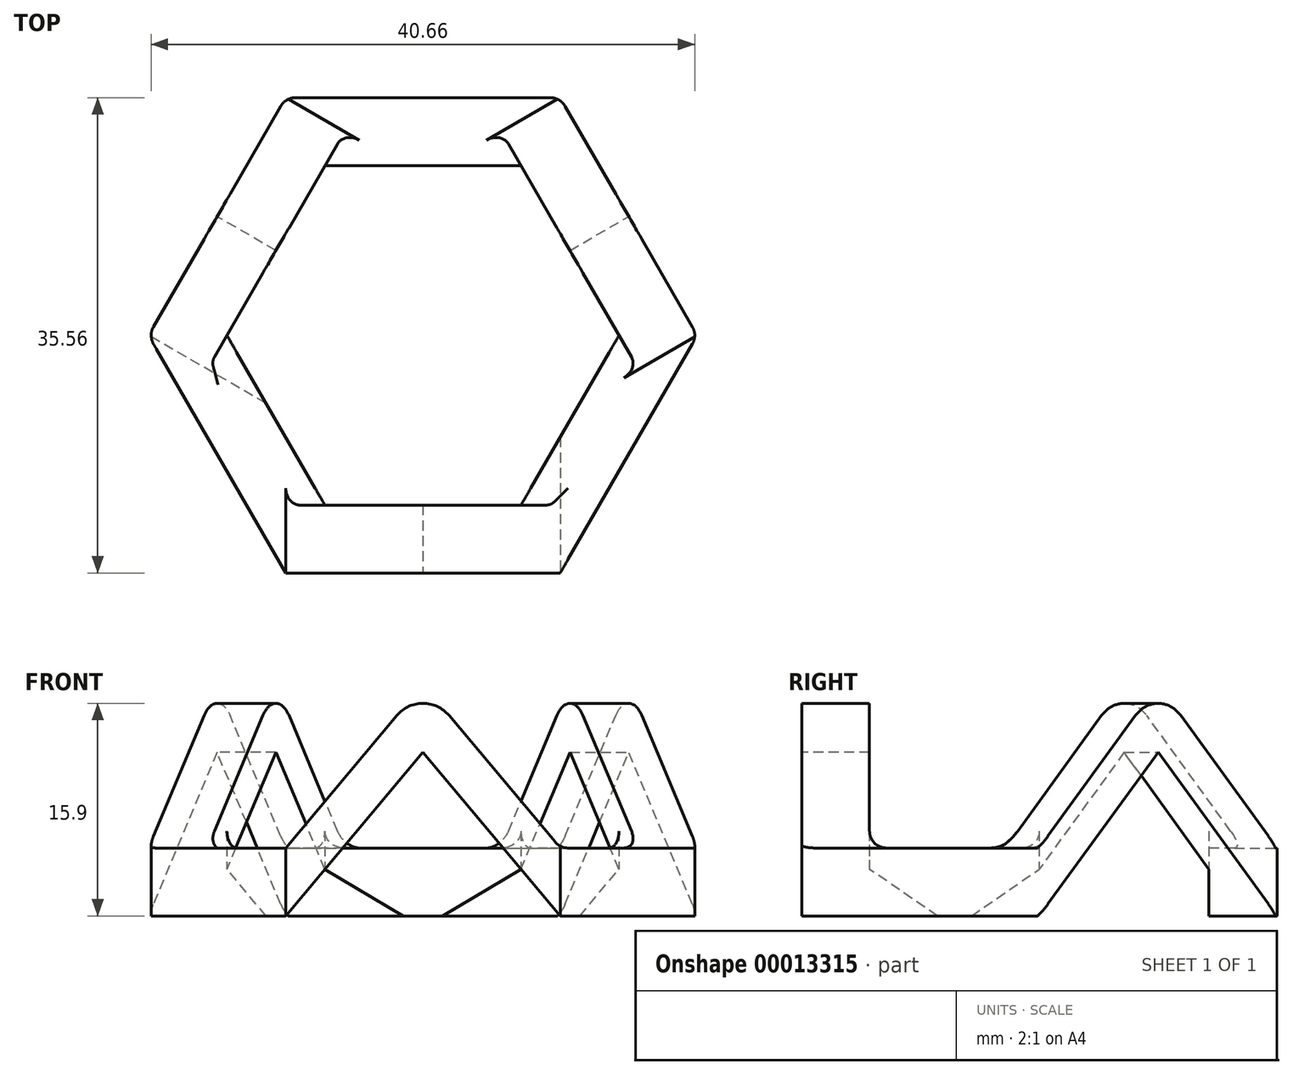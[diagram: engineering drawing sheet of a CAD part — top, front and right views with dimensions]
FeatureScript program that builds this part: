
annotation { "Feature Type Name" : "Feature", "Feature Type Description" : "" }
export const myFeature = defineFeature(function(context is Context, id is Id, definition is map)
    precondition{}
    {
        {
            var Q0;
            Q0=qCreatedBy(makeId("Top.planeOp"),FACE);
            var sketch = newSketch(context, id + "F0", { "sketchPlane" : qUnion([Q0])});
            skCircle(sketch, "E0.cCircle", {"center": v(0, 0) * mm, "radius": 12.7 * mm, "construction": true});
            skLineSegment(sketch, "E0.0", {"start": v(-7.33, 12.7) * mm, "end": v(7.33, 12.7) * mm});
            skLineSegment(sketch, "E0.1", {"start": v(7.33, 12.7) * mm, "end": v(14.66, 0) * mm});
            skLineSegment(sketch, "E0.2", {"start": v(14.66, 0) * mm, "end": v(7.33, -12.7) * mm});
            skLineSegment(sketch, "E0.3", {"start": v(7.33, -12.7) * mm, "end": v(-7.33, -12.7) * mm});
            skLineSegment(sketch, "E0.4", {"start": v(-7.33, -12.7) * mm, "end": v(-14.66, 0) * mm});
            skLineSegment(sketch, "E0.5", {"start": v(-14.66, 0) * mm, "end": v(-7.33, 12.7) * mm});
            skPoint(sketch, "E0.0.midPoint", {"position": v(0, 12.7) * mm});
            skLineSegment(sketch, "E1.0", {"start": v(-20.53, 0) * mm, "end": v(-10.27, 17.78) * mm});
            skLineSegment(sketch, "E1.1", {"start": v(-10.27, -17.78) * mm, "end": v(-20.53, 0) * mm});
            skLineSegment(sketch, "E1.2", {"start": v(10.27, -17.78) * mm, "end": v(-10.27, -17.78) * mm});
            skLineSegment(sketch, "E1.3", {"start": v(20.53, 0) * mm, "end": v(10.27, -17.78) * mm});
            skLineSegment(sketch, "E1.4", {"start": v(10.27, 17.78) * mm, "end": v(20.53, 0) * mm});
            skLineSegment(sketch, "E1.5", {"start": v(-10.27, 17.78) * mm, "end": v(10.27, 17.78) * mm});
            skSolve(sketch);
        }
        {
            var Q0;
            Q0=makeQuery(id+"F0.imprint","IMPRINT",FACE,{"disambiguationData":[TD([[makeQuery(id+"F0.imprint","IMPRINT",EDGE,{"derivedFrom":sQuery(id+"F0.wireOp",EDGE,"E0.0")}),1.0]])]});
            extrude(context, id + "F1", {"entities" : qUnion([Q0]), "depth" : 5.08 * mm});
        }
        {
            var Q0;
            Q0=makeQuery(id+"F1.opExtrude","SWEPT_FACE",FACE,{"disambiguationData":[OSD([sQuery(id+"F0.wireOp",EDGE,"E1.4")])]});
            var sketch = newSketch(context, id + "F2", { "sketchPlane" : qUnion([Q0])});
            skLineSegment(sketch, "E2", {"start": v(-10.27, 0) * mm, "end": v(0, 12.23) * mm});
            skLineSegment(sketch, "E3", {"start": v(10.27, 0) * mm, "end": v(0, 12.23) * mm});
            skLineSegment(sketch, "E4", {"start": v(-10.27, 5.08) * mm, "end": v(0, 17.31) * mm});
            skLineSegment(sketch, "E5", {"start": v(10.27, 5.08) * mm, "end": v(0, 17.31) * mm});
            skSolve(sketch);
        }
        {
            var Q0;
            {var subQ7=sQuery(id+"F2.wireOp",EDGE,"E4");Q0=makeQuery(id+"F2.imprint","IMPRINT",FACE,{"disambiguationData":[TD([[makeQuery(id+"F2.imprint","IMPRINT",EDGE,{"derivedFrom":subQ7}),-1.0]])]});}
            var Q1;
            {var subQ0=sQuery(id+"F0.wireOp",EDGE,"E1.4");var subQ4=makeQuery(id+"F1.opExtrude","SWEPT_EDGE",EDGE,{"disambiguationData":[OSD([sQuery(id+"F0.wireOp",EDGE,"E1.3"),subQ0])]});Q1=makeQuery(id+"F2.imprint","IMPRINT",FACE,{"disambiguationData":[TD([[makeQuery(id+"F2.imprint","IMPRINT",EDGE,{"derivedFrom":subQ4}),1.0]])]});}
            var Q2;
            {var subQ0=sQuery(id+"F0.wireOp",EDGE,"E1.4");var subQ4=makeQuery(id+"F1.opExtrude","SWEPT_EDGE",EDGE,{"disambiguationData":[OSD([subQ0,sQuery(id+"F0.wireOp",EDGE,"E1.5")])]});Q2=makeQuery(id+"F2.imprint","IMPRINT",FACE,{"disambiguationData":[TD([[makeQuery(id+"F2.imprint","IMPRINT",EDGE,{"derivedFrom":subQ4}),-1.0]])]});}
            extrude(context, id + "F3", {"entities" : qUnion([Q0, Q1, Q2]), "operationType" : NewBodyOperationType.ADD, "oppositeDirection" : true, "depth" : 5.08 * mm});
        }
        {
            var Q0;
            {var subQ0=sQuery(id+"F0.wireOp",EDGE,"E1.4");Q0=makeQuery(id+"F3.boolean.opBoolean","MERGE",FACE,{"derivedFrom":[makeQuery(id+"F1.opExtrude","SWEPT_FACE",FACE,{"disambiguationData":[OSD([subQ0])]}),makeQuery(id+"F3.opExtrude","CAP_FACE",FACE,{"disambiguationData":[OSD([sQuery(id+"F0.wireOp",EDGE,"E1.3"),subQ0,sQuery(id+"F0.wireOp",EDGE,"E1.5"),sQuery(id+"F2.wireOp",EDGE,"E2"),sQuery(id+"F2.wireOp",EDGE,"E3"),sQuery(id+"F2.wireOp",EDGE,"E4"),sQuery(id+"F2.wireOp",EDGE,"E5")])],"isStart":true})]});}
            var sketch = newSketch(context, id + "F4", { "sketchPlane" : qUnion([Q0])});
            skLineSegment(sketch, "E6", {"start": v(-10.27, 0) * mm, "end": v(-6, 5.08) * mm});
            skLineSegment(sketch, "E7", {"start": v(10.27, 0) * mm, "end": v(6, 5.08) * mm});
            skSolve(sketch);
        }
        {
            var Q0;
            Q0=makeQuery(id+"F4.imprint","IMPRINT",FACE,{"disambiguationData":[TD([[makeQuery(id+"F4.imprint","IMPRINT",EDGE,{"derivedFrom":sQuery(id+"F4.wireOp",EDGE,"E6")}),-1.0]])]});
            extrude(context, id + "F5", {"entities" : qUnion([Q0]), "operationType" : NewBodyOperationType.REMOVE, "oppositeDirection" : true, "depth" : 10.16 * mm});
        }
        {
            var Q0;
            Q0=makeQuery(id+"F1.opExtrude","SWEPT_FACE",FACE,{"disambiguationData":[OSD([sQuery(id+"F0.wireOp",EDGE,"E1.0")])]});
            var sketch = newSketch(context, id + "F6", { "sketchPlane" : qUnion([Q0])});
            skLineSegment(sketch, "E8", {"start": v(-10.27, 0) * mm, "end": v(0, 12.23) * mm});
            skLineSegment(sketch, "E9", {"start": v(0, 12.23) * mm, "end": v(10.27, 0) * mm});
            skLineSegment(sketch, "E10", {"start": v(-10.27, 5.08) * mm, "end": v(0, 17.31) * mm});
            skLineSegment(sketch, "E11", {"start": v(0, 17.31) * mm, "end": v(10.27, 5.08) * mm});
            skSolve(sketch);
        }
        {
            var Q0;
            {var subQ7=sQuery(id+"F6.wireOp",EDGE,"E10");Q0=makeQuery(id+"F6.imprint","IMPRINT",FACE,{"disambiguationData":[TD([[makeQuery(id+"F6.imprint","IMPRINT",EDGE,{"derivedFrom":subQ7}),-1.0]])]});}
            var Q1;
            {var subQ0=sQuery(id+"F0.wireOp",EDGE,"E1.0");var subQ4=makeQuery(id+"F1.opExtrude","SWEPT_EDGE",EDGE,{"disambiguationData":[OSD([subQ0,sQuery(id+"F0.wireOp",EDGE,"E1.5")])]});Q1=makeQuery(id+"F6.imprint","IMPRINT",FACE,{"disambiguationData":[TD([[makeQuery(id+"F6.imprint","IMPRINT",EDGE,{"derivedFrom":subQ4}),1.0]])]});}
            var Q2;
            {var subQ0=sQuery(id+"F0.wireOp",EDGE,"E1.0");var subQ4=makeQuery(id+"F1.opExtrude","SWEPT_EDGE",EDGE,{"disambiguationData":[OSD([subQ0,sQuery(id+"F0.wireOp",EDGE,"E1.1")])]});Q2=makeQuery(id+"F6.imprint","IMPRINT",FACE,{"disambiguationData":[TD([[makeQuery(id+"F6.imprint","IMPRINT",EDGE,{"derivedFrom":subQ4}),-1.0]])]});}
            extrude(context, id + "F7", {"entities" : qUnion([Q0, Q1, Q2]), "operationType" : NewBodyOperationType.ADD, "oppositeDirection" : true, "depth" : 5.08 * mm});
        }
        {
            var Q0;
            {var subQ0=sQuery(id+"F0.wireOp",EDGE,"E1.0");Q0=makeQuery(id+"F7.boolean.opBoolean","MERGE",FACE,{"derivedFrom":[makeQuery(id+"F1.opExtrude","SWEPT_FACE",FACE,{"disambiguationData":[OSD([subQ0])]}),makeQuery(id+"F7.opExtrude","CAP_FACE",FACE,{"disambiguationData":[OSD([subQ0,sQuery(id+"F0.wireOp",EDGE,"E1.1"),sQuery(id+"F0.wireOp",EDGE,"E1.5"),sQuery(id+"F6.wireOp",EDGE,"E8"),sQuery(id+"F6.wireOp",EDGE,"E9"),sQuery(id+"F6.wireOp",EDGE,"E10"),sQuery(id+"F6.wireOp",EDGE,"E11")])],"isStart":true})]});}
            var sketch = newSketch(context, id + "F8", { "sketchPlane" : qUnion([Q0])});
            skLineSegment(sketch, "E12", {"start": v(-10.27, 0) * mm, "end": v(-6, 5.08) * mm});
            skLineSegment(sketch, "E13", {"start": v(10.27, 0) * mm, "end": v(6, 5.08) * mm});
            skSolve(sketch);
        }
        {
            var Q0;
            Q0 = qSketchRegion(id + "F8", true);
            var Q1;
            Q1=makeQuery(id+"F8.imprint","IMPRINT",FACE,{"disambiguationData":[TD([[makeQuery(id+"F8.imprint","IMPRINT",EDGE,{"derivedFrom":sQuery(id+"F8.wireOp",EDGE,"E12")}),-1.0]])]});
            extrude(context, id + "F9", {"entities" : qUnion([Q0, Q1]), "operationType" : NewBodyOperationType.REMOVE, "oppositeDirection" : true, "depth" : 12.7 * mm});
        }
        {
            var Q0;
            Q0=makeQuery(id+"F1.opExtrude","SWEPT_FACE",FACE,{"disambiguationData":[OSD([sQuery(id+"F0.wireOp",EDGE,"E1.2")])]});
            var sketch = newSketch(context, id + "F10", { "sketchPlane" : qUnion([Q0])});
            skLineSegment(sketch, "E14", {"start": v(-10.27, 0) * mm, "end": v(0, 12.23) * mm});
            skLineSegment(sketch, "E15", {"start": v(0, 12.23) * mm, "end": v(10.27, 0) * mm});
            skLineSegment(sketch, "E16", {"start": v(-10.27, 5.08) * mm, "end": v(0, 17.31) * mm});
            skLineSegment(sketch, "E17", {"start": v(0, 17.31) * mm, "end": v(10.27, 5.08) * mm});
            skSolve(sketch);
        }
        {
            var Q0;
            Q0 = qSketchRegion(id + "F10", true);
            var Q1;
            {var subQ7=sQuery(id+"F10.wireOp",EDGE,"E16");Q1=makeQuery(id+"F10.imprint","IMPRINT",FACE,{"disambiguationData":[TD([[makeQuery(id+"F10.imprint","IMPRINT",EDGE,{"derivedFrom":subQ7}),-1.0]])]});}
            var Q2;
            {var subQ0=sQuery(id+"F0.wireOp",EDGE,"E1.2");var subQ4=makeQuery(id+"F1.opExtrude","SWEPT_EDGE",EDGE,{"disambiguationData":[OSD([sQuery(id+"F0.wireOp",EDGE,"E1.1"),subQ0])]});Q2=makeQuery(id+"F10.imprint","IMPRINT",FACE,{"disambiguationData":[TD([[makeQuery(id+"F10.imprint","IMPRINT",EDGE,{"derivedFrom":subQ4}),1.0]])]});}
            var Q3;
            {var subQ0=sQuery(id+"F0.wireOp",EDGE,"E1.2");var subQ4=makeQuery(id+"F1.opExtrude","SWEPT_EDGE",EDGE,{"disambiguationData":[OSD([subQ0,sQuery(id+"F0.wireOp",EDGE,"E1.3")])]});Q3=makeQuery(id+"F10.imprint","IMPRINT",FACE,{"disambiguationData":[TD([[makeQuery(id+"F10.imprint","IMPRINT",EDGE,{"derivedFrom":subQ4}),-1.0]])]});}
            extrude(context, id + "F11", {"entities" : qUnion([Q0, Q1, Q2, Q3]), "operationType" : NewBodyOperationType.ADD, "oppositeDirection" : true, "depth" : 5.08 * mm});
        }
        {
            var Q0;
            {var subQ0=sQuery(id+"F0.wireOp",EDGE,"E1.2");Q0=makeQuery(id+"F11.boolean.opBoolean","MERGE",FACE,{"derivedFrom":[makeQuery(id+"F1.opExtrude","SWEPT_FACE",FACE,{"disambiguationData":[OSD([subQ0])]}),makeQuery(id+"F11.opExtrude","CAP_FACE",FACE,{"disambiguationData":[OSD([sQuery(id+"F0.wireOp",EDGE,"E1.1"),subQ0,sQuery(id+"F0.wireOp",EDGE,"E1.3"),sQuery(id+"F10.wireOp",EDGE,"E14"),sQuery(id+"F10.wireOp",EDGE,"E15"),sQuery(id+"F10.wireOp",EDGE,"E16"),sQuery(id+"F10.wireOp",EDGE,"E17")])],"isStart":true})]});}
            var sketch = newSketch(context, id + "F12", { "sketchPlane" : qUnion([Q0])});
            skLineSegment(sketch, "E18", {"start": v(-10.27, 0) * mm, "end": v(-6, 5.08) * mm});
            skLineSegment(sketch, "E19", {"start": v(10.27, 0) * mm, "end": v(6, 5.08) * mm});
            skSolve(sketch);
        }
        {
            var Q0;
            Q0 = qSketchRegion(id + "F12", true);
            var Q1;
            Q1=makeQuery(id+"F12.imprint","IMPRINT",FACE,{"disambiguationData":[TD([[makeQuery(id+"F12.imprint","IMPRINT",EDGE,{"derivedFrom":sQuery(id+"F12.wireOp",EDGE,"E18")}),-1.0]])]});
            extrude(context, id + "F13", {"entities" : qUnion([Q0, Q1]), "operationType" : NewBodyOperationType.REMOVE, "oppositeDirection" : true, "depth" : 12.7 * mm});
        }
        {
            var Q0;
            Q0=makeQuery(id+"F11.opExtrude","SWEPT_EDGE",EDGE,{"disambiguationData":[OSD([sQuery(id+"F10.wireOp",EDGE,"E16"),sQuery(id+"F10.wireOp",EDGE,"E17")])]});
            var Q1;
            Q1=makeQuery(id+"F7.opExtrude","SWEPT_EDGE",EDGE,{"disambiguationData":[OSD([sQuery(id+"F6.wireOp",EDGE,"E10"),sQuery(id+"F6.wireOp",EDGE,"E11")])]});
            var Q2;
            Q2=makeQuery(id+"F3.opExtrude","SWEPT_EDGE",EDGE,{"disambiguationData":[OSD([sQuery(id+"F2.wireOp",EDGE,"E4"),sQuery(id+"F2.wireOp",EDGE,"E5")])]});
            fillet(context, id + "F14", {"entities" : qUnion([Q0, Q1, Q2]), "radius" : 2.54 * mm, "tangentPropagation" : true, "allowEdgeOverflow" : false});
        }
        {
            var Q0;
            Q0=makeQuery(id+"F3.opExtrude","SWEPT_EDGE",EDGE,{"disambiguationData":[OSD([sQuery(id+"F0.wireOp",EDGE,"E1.4"),sQuery(id+"F0.wireOp",EDGE,"E1.5"),sQuery(id+"F2.wireOp",EDGE,"E5")])]});
            var Q1;
            Q1=makeQuery(id+"F7.opExtrude","SWEPT_EDGE",EDGE,{"disambiguationData":[OSD([sQuery(id+"F0.wireOp",EDGE,"E1.0"),sQuery(id+"F0.wireOp",EDGE,"E1.5"),sQuery(id+"F6.wireOp",EDGE,"E10")])]});
            var Q2;
            Q2=makeQuery(id+"F1.opExtrude","SWEPT_EDGE",EDGE,{"disambiguationData":[OSD([sQuery(id+"F0.wireOp",EDGE,"E1.0"),sQuery(id+"F0.wireOp",EDGE,"E1.5")])]});
            var Q3;
            Q3=makeQuery(id+"F1.opExtrude","SWEPT_EDGE",EDGE,{"disambiguationData":[OSD([sQuery(id+"F0.wireOp",EDGE,"E1.4"),sQuery(id+"F0.wireOp",EDGE,"E1.5")])]});
            var Q4;
            Q4=makeQuery(id+"F1.opExtrude","SWEPT_EDGE",EDGE,{"disambiguationData":[OSD([sQuery(id+"F0.wireOp",EDGE,"E1.0"),sQuery(id+"F0.wireOp",EDGE,"E1.1")])]});
            var Q5;
            Q5=makeQuery(id+"F1.opExtrude","SWEPT_EDGE",EDGE,{"disambiguationData":[OSD([sQuery(id+"F0.wireOp",EDGE,"E1.3"),sQuery(id+"F0.wireOp",EDGE,"E1.4")])]});
            var Q6;
            Q6=makeQuery(id+"F11.opExtrude","SWEPT_EDGE",EDGE,{"disambiguationData":[OSD([sQuery(id+"F0.wireOp",EDGE,"E1.2"),sQuery(id+"F0.wireOp",EDGE,"E1.3"),sQuery(id+"F10.wireOp",EDGE,"E17")])]});
            var Q7;
            {var subQ0=sQuery(id+"F0.wireOp",EDGE,"E0.0");var subQ1=sQuery(id+"F0.wireOp",EDGE,"E0.1");var subQ2=sQuery(id+"F0.wireOp",EDGE,"E0.2");var subQ3=sQuery(id+"F0.wireOp",EDGE,"E0.3");var subQ4=sQuery(id+"F0.wireOp",EDGE,"E0.4");var subQ5=sQuery(id+"F0.wireOp",EDGE,"E0.5");var subQ6=sQuery(id+"F0.wireOp",EDGE,"E1.0");var subQ7=sQuery(id+"F0.wireOp",EDGE,"E1.1");var subQ8=sQuery(id+"F0.wireOp",EDGE,"E1.2");var subQ9=sQuery(id+"F0.wireOp",EDGE,"E1.3");var subQ10=sQuery(id+"F0.wireOp",EDGE,"E1.4");var subQ11=sQuery(id+"F0.wireOp",EDGE,"E1.5");var subQ27=makeQuery(id+"F1.opExtrude","SWEPT_FACE",FACE,{"disambiguationData":[OSD([subQ2])]});Q7=makeQuery(id+"F11.boolean.opBoolean","INTERSECT",EDGE,{"disambiguationData":[OD(0.0)],"derivedFrom":[makeQuery(id+"F7.boolean.opBoolean","SPLIT",FACE,{"disambiguationData":[TD([subQ27])],"derivedFrom":makeQuery(id+"F3.boolean.opBoolean","SPLIT",FACE,{"disambiguationData":[TD([makeQuery(id+"F1.opExtrude","SWEPT_FACE",FACE,{"disambiguationData":[OSD([subQ0])]})])],"derivedFrom":makeQuery(id+"F1.opExtrude","CAP_FACE",FACE,{"disambiguationData":[OSD([subQ0,subQ1,subQ2,subQ3,subQ4,subQ5,subQ6,subQ7,subQ8,subQ9,subQ10,subQ11])],"isStart":false})})}),makeQuery(id+"F11.opExtrude","CAP_FACE",FACE,{"disambiguationData":[OSD([subQ7,subQ8,subQ9,sQuery(id+"F10.wireOp",EDGE,"E14"),sQuery(id+"F10.wireOp",EDGE,"E15"),sQuery(id+"F10.wireOp",EDGE,"E16"),sQuery(id+"F10.wireOp",EDGE,"E17")])],"isStart":false})]});}
            var Q8;
            {var subQ0=sQuery(id+"F0.wireOp",EDGE,"E0.0");var subQ1=sQuery(id+"F0.wireOp",EDGE,"E0.1");var subQ2=sQuery(id+"F0.wireOp",EDGE,"E0.2");var subQ3=sQuery(id+"F0.wireOp",EDGE,"E0.3");var subQ4=sQuery(id+"F0.wireOp",EDGE,"E0.4");var subQ5=sQuery(id+"F0.wireOp",EDGE,"E0.5");var subQ6=sQuery(id+"F0.wireOp",EDGE,"E1.0");var subQ7=sQuery(id+"F0.wireOp",EDGE,"E1.1");var subQ8=sQuery(id+"F0.wireOp",EDGE,"E1.2");var subQ9=sQuery(id+"F0.wireOp",EDGE,"E1.3");var subQ10=sQuery(id+"F0.wireOp",EDGE,"E1.4");var subQ11=sQuery(id+"F0.wireOp",EDGE,"E1.5");var subQ27=makeQuery(id+"F1.opExtrude","SWEPT_FACE",FACE,{"disambiguationData":[OSD([subQ2])]});Q8=makeQuery(id+"F11.boolean.opBoolean","INTERSECT",EDGE,{"disambiguationData":[OD(1.0)],"derivedFrom":[makeQuery(id+"F7.boolean.opBoolean","SPLIT",FACE,{"disambiguationData":[TD([subQ27])],"derivedFrom":makeQuery(id+"F3.boolean.opBoolean","SPLIT",FACE,{"disambiguationData":[TD([makeQuery(id+"F1.opExtrude","SWEPT_FACE",FACE,{"disambiguationData":[OSD([subQ0])]})])],"derivedFrom":makeQuery(id+"F1.opExtrude","CAP_FACE",FACE,{"disambiguationData":[OSD([subQ0,subQ1,subQ2,subQ3,subQ4,subQ5,subQ6,subQ7,subQ8,subQ9,subQ10,subQ11])],"isStart":false})})}),makeQuery(id+"F11.opExtrude","CAP_FACE",FACE,{"disambiguationData":[OSD([subQ7,subQ8,subQ9,sQuery(id+"F10.wireOp",EDGE,"E14"),sQuery(id+"F10.wireOp",EDGE,"E15"),sQuery(id+"F10.wireOp",EDGE,"E16"),sQuery(id+"F10.wireOp",EDGE,"E17")])],"isStart":false})]});}
            var Q9;
            Q9=makeQuery(id+"F11.opExtrude","SWEPT_EDGE",EDGE,{"disambiguationData":[OSD([sQuery(id+"F0.wireOp",EDGE,"E1.1"),sQuery(id+"F0.wireOp",EDGE,"E1.2"),sQuery(id+"F10.wireOp",EDGE,"E16")])]});
            var Q10;
            Q10=makeQuery(id+"F7.opExtrude","SWEPT_EDGE",EDGE,{"disambiguationData":[OSD([sQuery(id+"F0.wireOp",EDGE,"E1.0"),sQuery(id+"F0.wireOp",EDGE,"E1.1"),sQuery(id+"F6.wireOp",EDGE,"E11")])]});
            var Q11;
            {var subQ0=sQuery(id+"F0.wireOp",EDGE,"E1.3");var subQ1=sQuery(id+"F0.wireOp",EDGE,"E1.4");var subQ2=sQuery(id+"F0.wireOp",EDGE,"E1.5");Q11=makeQuery(id+"F3.boolean.opBoolean","INTERSECT",EDGE,{"disambiguationData":[OD(1.0)],"derivedFrom":[makeQuery(id+"F1.opExtrude","CAP_FACE",FACE,{"disambiguationData":[OSD([sQuery(id+"F0.wireOp",EDGE,"E0.0"),sQuery(id+"F0.wireOp",EDGE,"E0.1"),sQuery(id+"F0.wireOp",EDGE,"E0.2"),sQuery(id+"F0.wireOp",EDGE,"E0.3"),sQuery(id+"F0.wireOp",EDGE,"E0.4"),sQuery(id+"F0.wireOp",EDGE,"E0.5"),sQuery(id+"F0.wireOp",EDGE,"E1.0"),sQuery(id+"F0.wireOp",EDGE,"E1.1"),sQuery(id+"F0.wireOp",EDGE,"E1.2"),subQ0,subQ1,subQ2])],"isStart":false}),makeQuery(id+"F3.opExtrude","CAP_FACE",FACE,{"disambiguationData":[OSD([subQ0,subQ1,subQ2,sQuery(id+"F2.wireOp",EDGE,"E2"),sQuery(id+"F2.wireOp",EDGE,"E3"),sQuery(id+"F2.wireOp",EDGE,"E4"),sQuery(id+"F2.wireOp",EDGE,"E5")])],"isStart":false})]});}
            var Q12;
            Q12=makeQuery(id+"F3.opExtrude","SWEPT_EDGE",EDGE,{"disambiguationData":[OSD([sQuery(id+"F0.wireOp",EDGE,"E1.3"),sQuery(id+"F0.wireOp",EDGE,"E1.4"),sQuery(id+"F2.wireOp",EDGE,"E4")])]});
            var Q13;
            {var subQ0=sQuery(id+"F0.wireOp",EDGE,"E0.0");var subQ1=sQuery(id+"F0.wireOp",EDGE,"E0.1");var subQ2=sQuery(id+"F0.wireOp",EDGE,"E0.2");var subQ3=sQuery(id+"F0.wireOp",EDGE,"E0.3");var subQ4=sQuery(id+"F0.wireOp",EDGE,"E0.4");var subQ5=sQuery(id+"F0.wireOp",EDGE,"E0.5");var subQ6=sQuery(id+"F0.wireOp",EDGE,"E1.0");var subQ7=sQuery(id+"F0.wireOp",EDGE,"E1.1");var subQ8=sQuery(id+"F0.wireOp",EDGE,"E1.2");var subQ9=sQuery(id+"F0.wireOp",EDGE,"E1.3");var subQ10=sQuery(id+"F0.wireOp",EDGE,"E1.4");var subQ11=sQuery(id+"F0.wireOp",EDGE,"E1.5");Q13=makeQuery(id+"F7.boolean.opBoolean","INTERSECT",EDGE,{"disambiguationData":[OD(1.0)],"derivedFrom":[makeQuery(id+"F3.boolean.opBoolean","SPLIT",FACE,{"disambiguationData":[TD([makeQuery(id+"F1.opExtrude","SWEPT_FACE",FACE,{"disambiguationData":[OSD([subQ0])]})])],"derivedFrom":makeQuery(id+"F1.opExtrude","CAP_FACE",FACE,{"disambiguationData":[OSD([subQ0,subQ1,subQ2,subQ3,subQ4,subQ5,subQ6,subQ7,subQ8,subQ9,subQ10,subQ11])],"isStart":false})}),makeQuery(id+"F7.opExtrude","CAP_FACE",FACE,{"disambiguationData":[OSD([subQ6,subQ7,subQ11,sQuery(id+"F6.wireOp",EDGE,"E8"),sQuery(id+"F6.wireOp",EDGE,"E9"),sQuery(id+"F6.wireOp",EDGE,"E10"),sQuery(id+"F6.wireOp",EDGE,"E11")])],"isStart":false})]});}
            var Q14;
            {var subQ0=sQuery(id+"F0.wireOp",EDGE,"E0.0");var subQ1=sQuery(id+"F0.wireOp",EDGE,"E0.1");var subQ2=sQuery(id+"F0.wireOp",EDGE,"E0.2");var subQ3=sQuery(id+"F0.wireOp",EDGE,"E0.3");var subQ4=sQuery(id+"F0.wireOp",EDGE,"E0.4");var subQ5=sQuery(id+"F0.wireOp",EDGE,"E0.5");var subQ6=sQuery(id+"F0.wireOp",EDGE,"E1.0");var subQ7=sQuery(id+"F0.wireOp",EDGE,"E1.1");var subQ8=sQuery(id+"F0.wireOp",EDGE,"E1.2");var subQ9=sQuery(id+"F0.wireOp",EDGE,"E1.3");var subQ10=sQuery(id+"F0.wireOp",EDGE,"E1.4");var subQ11=sQuery(id+"F0.wireOp",EDGE,"E1.5");Q14=makeQuery(id+"F7.boolean.opBoolean","INTERSECT",EDGE,{"disambiguationData":[OD(0.0)],"derivedFrom":[makeQuery(id+"F3.boolean.opBoolean","SPLIT",FACE,{"disambiguationData":[TD([makeQuery(id+"F1.opExtrude","SWEPT_FACE",FACE,{"disambiguationData":[OSD([subQ0])]})])],"derivedFrom":makeQuery(id+"F1.opExtrude","CAP_FACE",FACE,{"disambiguationData":[OSD([subQ0,subQ1,subQ2,subQ3,subQ4,subQ5,subQ6,subQ7,subQ8,subQ9,subQ10,subQ11])],"isStart":false})}),makeQuery(id+"F7.opExtrude","CAP_FACE",FACE,{"disambiguationData":[OSD([subQ6,subQ7,subQ11,sQuery(id+"F6.wireOp",EDGE,"E8"),sQuery(id+"F6.wireOp",EDGE,"E9"),sQuery(id+"F6.wireOp",EDGE,"E10"),sQuery(id+"F6.wireOp",EDGE,"E11")])],"isStart":false})]});}
            var Q15;
            {var subQ0=sQuery(id+"F0.wireOp",EDGE,"E1.3");var subQ1=sQuery(id+"F0.wireOp",EDGE,"E1.4");var subQ2=sQuery(id+"F0.wireOp",EDGE,"E1.5");Q15=makeQuery(id+"F3.boolean.opBoolean","INTERSECT",EDGE,{"disambiguationData":[OD(0.0)],"derivedFrom":[makeQuery(id+"F1.opExtrude","CAP_FACE",FACE,{"disambiguationData":[OSD([sQuery(id+"F0.wireOp",EDGE,"E0.0"),sQuery(id+"F0.wireOp",EDGE,"E0.1"),sQuery(id+"F0.wireOp",EDGE,"E0.2"),sQuery(id+"F0.wireOp",EDGE,"E0.3"),sQuery(id+"F0.wireOp",EDGE,"E0.4"),sQuery(id+"F0.wireOp",EDGE,"E0.5"),sQuery(id+"F0.wireOp",EDGE,"E1.0"),sQuery(id+"F0.wireOp",EDGE,"E1.1"),sQuery(id+"F0.wireOp",EDGE,"E1.2"),subQ0,subQ1,subQ2])],"isStart":false}),makeQuery(id+"F3.opExtrude","CAP_FACE",FACE,{"disambiguationData":[OSD([subQ0,subQ1,subQ2,sQuery(id+"F2.wireOp",EDGE,"E2"),sQuery(id+"F2.wireOp",EDGE,"E3"),sQuery(id+"F2.wireOp",EDGE,"E4"),sQuery(id+"F2.wireOp",EDGE,"E5")])],"isStart":false})]});}
            fillet(context, id + "F15", {"entities" : qUnion([Q0, Q1, Q2, Q3, Q4, Q5, Q6, Q7, Q8, Q9, Q10, Q11, Q12, Q13, Q14, Q15]), "radius" : 1.27 * mm, "tangentPropagation" : true, "allowEdgeOverflow" : false});
        }
    });
